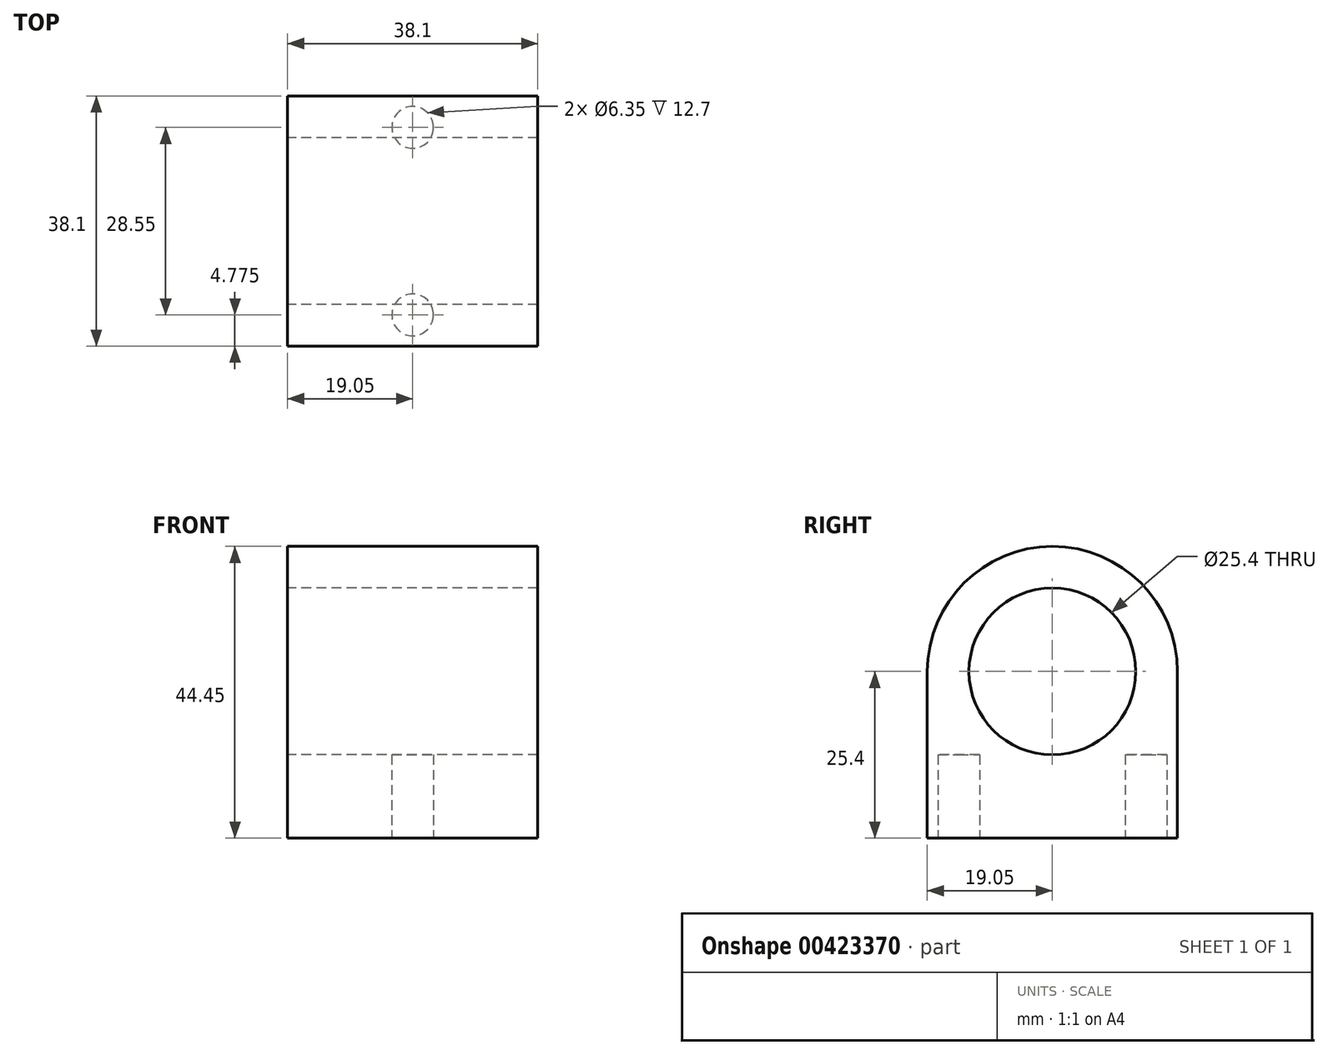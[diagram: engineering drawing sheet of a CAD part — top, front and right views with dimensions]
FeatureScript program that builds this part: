
annotation { "Feature Type Name" : "Feature", "Feature Type Description" : "" }
export const myFeature = defineFeature(function(context is Context, id is Id, definition is map)
    precondition{}
    {
        {
            var Q0;
            Q0=qCreatedBy(makeId("Right.planeOp"),FACE);
            var sketch = newSketch(context, id + "F0", { "sketchPlane" : qUnion([Q0])});
            skCircle(sketch, "E0", {"center": v(0, 0) * mm, "radius": 12.7 * mm});
            skCircle(sketch, "E1", {"center": v(0, 0) * mm, "radius": 19.05 * mm});
            skLineSegment(sketch, "E2.bottom", {"start": v(-19.05, 0) * mm, "end": v(19.05, 0) * mm});
            skLineSegment(sketch, "E2.top", {"start": v(-19.05, -25.4) * mm, "end": v(19.05, -25.4) * mm});
            skLineSegment(sketch, "E2.left", {"start": v(-19.05, 0) * mm, "end": v(-19.05, -25.4) * mm});
            skLineSegment(sketch, "E2.right", {"start": v(19.05, 0) * mm, "end": v(19.05, -25.4) * mm});
            skSolve(sketch);
        }
        {
            var Q0;
            Q0 = qSketchRegion(id + "F0", true);
            extrude(context, id + "F1", {"entities" : qUnion([Q0]), "endBound" : BoundingType.SYMMETRIC, "depth" : 38.1 * mm});
        }
        {
            var Q0;
            Q0=makeQuery(id+"F1.opExtrude","SWEPT_FACE",FACE,{"disambiguationData":[OSD([sQuery(id+"F0.wireOp",EDGE,"E2.top")])]});
            var sketch = newSketch(context, id + "F2", { "sketchPlane" : qUnion([Q0])});
            skCircle(sketch, "E3", {"center": v(0, 14.27) * mm, "radius": 3.18 * mm});
            skCircle(sketch, "E4", {"center": v(0, -14.27) * mm, "radius": 3.18 * mm});
            skSolve(sketch);
        }
        {
            var Q0;
            Q0 = qSketchRegion(id + "F2", true);
            extrude(context, id + "F3", {"entities" : qUnion([Q0]), "operationType" : NewBodyOperationType.REMOVE, "oppositeDirection" : true, "depth" : 12.7 * mm});
        }
    });
